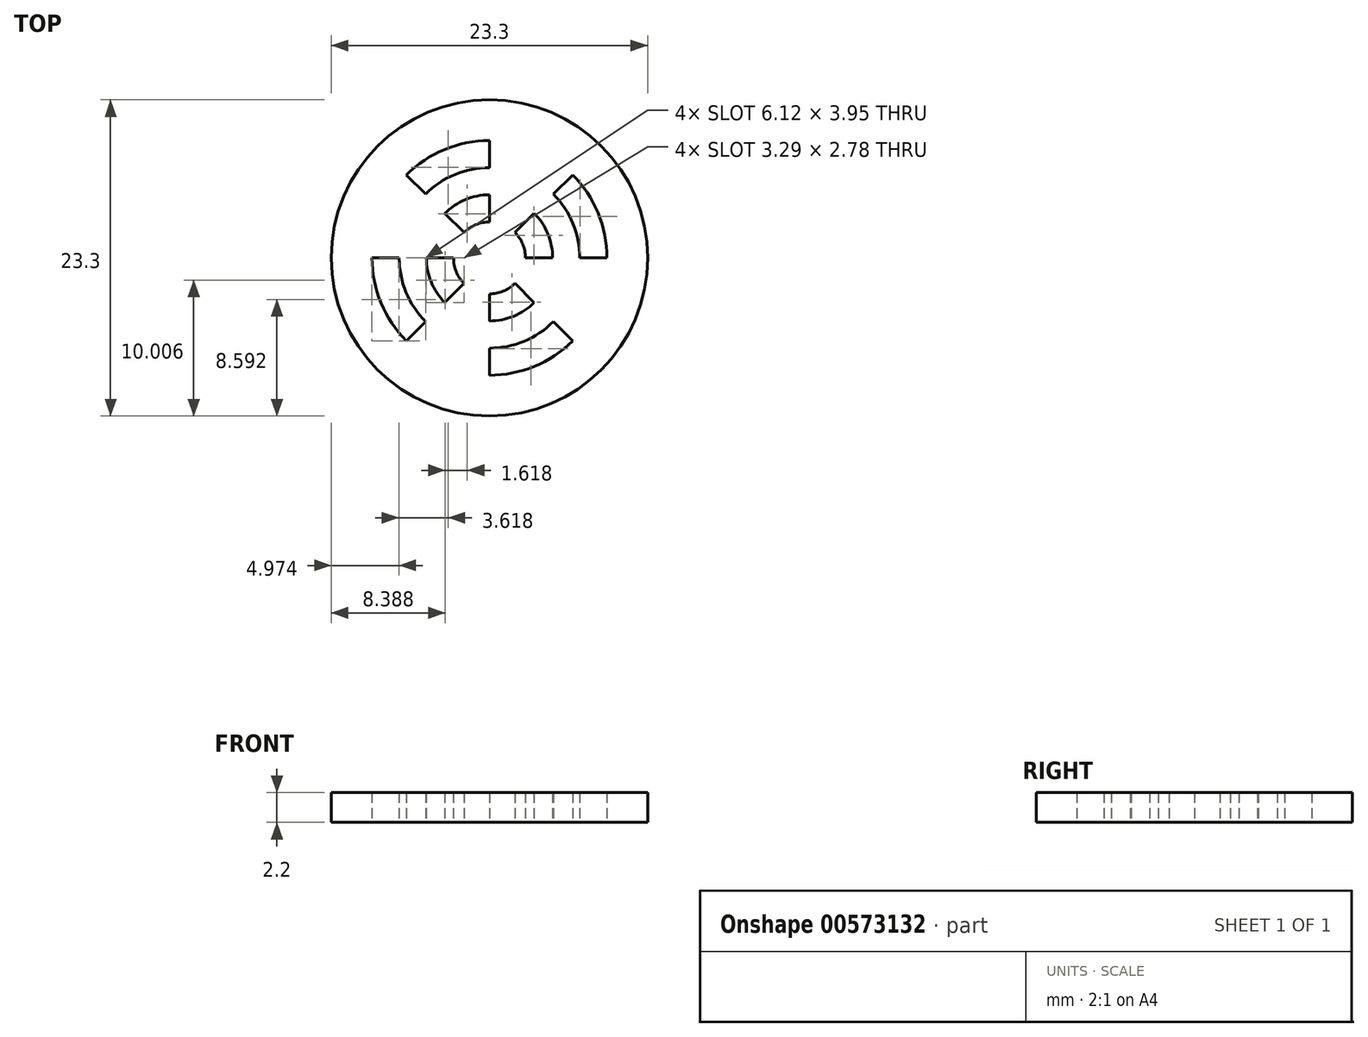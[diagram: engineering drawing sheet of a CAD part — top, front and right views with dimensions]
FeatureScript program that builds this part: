
annotation { "Feature Type Name" : "Feature", "Feature Type Description" : "" }
export const myFeature = defineFeature(function(context is Context, id is Id, definition is map)
    precondition{}
    {
        {
            var Q0;
            Q0=qCreatedBy(makeId("Top.planeOp"),FACE);
            var sketch = newSketch(context, id + "F0", { "sketchPlane" : qUnion([Q0])});
            skCircle(sketch, "E0", {"center": v(0, 0) * mm, "radius": 11.65 * mm});
            skSolve(sketch);
        }
        {
            var Q0;
            Q0=makeQuery(id+"F0.imprint","IMPRINT",FACE,{"disambiguationData":[TD([[makeQuery(id+"F0.imprint","IMPRINT",EDGE,{"derivedFrom":sQuery(id+"F0.wireOp",EDGE,"E0")}),1.0]])]});
            extrude(context, id + "F1", {"entities" : qUnion([Q0]), "depth" : 2.2 * mm, "offsetDistance" : 25 * mm});
        }
        {
            var Q0;
            Q0=makeQuery(id+"F1.opExtrude","CAP_FACE",FACE,{"disambiguationData":[OSD([sQuery(id+"F0.wireOp",EDGE,"E0")])],"isStart":true});
            var sketch = newSketch(context, id + "F2", { "sketchPlane" : qUnion([Q0])});
            skCircle(sketch, "E1", {"center": v(0, 0) * mm, "radius": 10.65 * mm});
            skCircle(sketch, "E2", {"center": v(0, 0) * mm, "radius": 8.65 * mm});
            skCircle(sketch, "E3", {"center": v(0, 0) * mm, "radius": 6.65 * mm});
            skCircle(sketch, "E4", {"center": v(0, 0) * mm, "radius": 4.65 * mm});
            skCircle(sketch, "E5", {"center": v(0, 0) * mm, "radius": 2.65 * mm});
            skLineSegment(sketch, "E6", {"start": v(-10.65, 0) * mm, "end": v(10.65, 0) * mm});
            skLineSegment(sketch, "E7", {"start": v(0, -10.65) * mm, "end": v(0, 10.65) * mm});
            skLineSegment(sketch, "E8", {"start": v(-10.65, 0) * mm, "end": v(0, 10.65) * mm, "construction": true});
            skLineSegment(sketch, "E9", {"start": v(-5.33, 5.33) * mm, "end": v(-9.71, 9.71) * mm, "construction": true});
            skLineSegment(sketch, "E10", {"start": v(-8.24, 8.24) * mm, "end": v(8.24, -8.24) * mm, "construction": true});
            skLineSegment(sketch, "E11", {"start": v(0, 0) * mm, "end": v(-8.24, -8.24) * mm});
            skLineSegment(sketch, "E12", {"start": v(0, 0) * mm, "end": v(7.53, 7.53) * mm});
            skLineSegment(sketch, "E13", {"start": v(7.53, -7.53) * mm, "end": v(-7.53, 7.53) * mm});
            skSolve(sketch);
        }
        {
            var Q0;
            {var subQ0=sQuery(id+"F2.wireOp",EDGE,"E11");var subQ1=sQuery(id+"F2.wireOp",EDGE,"E2");var subQ2=makeQuery(id+"F2.imprint","INTERSECT",VERTEX,{"derivedFrom":[subQ1,subQ0]});Q0=makeQuery(id+"F2.imprint","IMPRINT",FACE,{"disambiguationData":[TD([[makeQuery(id+"F2.imprint","IMPRINT",EDGE,{"disambiguationData":[TD([[subQ2,-1.0]])],"derivedFrom":subQ1}),1.0]])]});}
            var Q1;
            {var subQ0=sQuery(id+"F2.wireOp",EDGE,"E11");var subQ1=sQuery(id+"F2.wireOp",EDGE,"E4");var subQ2=makeQuery(id+"F2.imprint","INTERSECT",VERTEX,{"derivedFrom":[subQ1,subQ0]});Q1=makeQuery(id+"F2.imprint","IMPRINT",FACE,{"disambiguationData":[TD([[makeQuery(id+"F2.imprint","IMPRINT",EDGE,{"disambiguationData":[TD([[subQ2,-1.0]])],"derivedFrom":subQ1}),1.0]])]});}
            var Q2;
            {var subQ0=sQuery(id+"F2.wireOp",EDGE,"E6");var subQ1=sQuery(id+"F2.wireOp",EDGE,"E2");var subQ2=makeQuery(id+"F2.imprint","INTERSECT",VERTEX,{"disambiguationData":[OD(0.0)],"derivedFrom":[subQ1,subQ0]});Q2=makeQuery(id+"F2.imprint","IMPRINT",FACE,{"disambiguationData":[TD([[makeQuery(id+"F2.imprint","IMPRINT",EDGE,{"disambiguationData":[TD([[subQ2,1.0]])],"derivedFrom":subQ1}),1.0]])]});}
            var Q3;
            {var subQ0=sQuery(id+"F2.wireOp",EDGE,"E6");var subQ1=sQuery(id+"F2.wireOp",EDGE,"E4");var subQ2=makeQuery(id+"F2.imprint","INTERSECT",VERTEX,{"disambiguationData":[OD(0.0)],"derivedFrom":[subQ1,subQ0]});Q3=makeQuery(id+"F2.imprint","IMPRINT",FACE,{"disambiguationData":[TD([[makeQuery(id+"F2.imprint","IMPRINT",EDGE,{"disambiguationData":[TD([[subQ2,1.0]])],"derivedFrom":subQ1}),1.0]])]});}
            var Q4;
            {var subQ0=sQuery(id+"F2.wireOp",EDGE,"E12");var subQ1=sQuery(id+"F2.wireOp",EDGE,"E2");var subQ2=makeQuery(id+"F2.imprint","INTERSECT",VERTEX,{"derivedFrom":[subQ1,subQ0]});Q4=makeQuery(id+"F2.imprint","IMPRINT",FACE,{"disambiguationData":[TD([[makeQuery(id+"F2.imprint","IMPRINT",EDGE,{"disambiguationData":[TD([[subQ2,-1.0]])],"derivedFrom":subQ1}),1.0]])]});}
            var Q5;
            {var subQ0=sQuery(id+"F2.wireOp",EDGE,"E12");var subQ1=sQuery(id+"F2.wireOp",EDGE,"E4");var subQ2=makeQuery(id+"F2.imprint","INTERSECT",VERTEX,{"derivedFrom":[subQ1,subQ0]});Q5=makeQuery(id+"F2.imprint","IMPRINT",FACE,{"disambiguationData":[TD([[makeQuery(id+"F2.imprint","IMPRINT",EDGE,{"disambiguationData":[TD([[subQ2,-1.0]])],"derivedFrom":subQ1}),1.0]])]});}
            var Q6;
            {var subQ0=sQuery(id+"F2.wireOp",EDGE,"E13");var subQ1=sQuery(id+"F2.wireOp",EDGE,"E4");var subQ2=makeQuery(id+"F2.imprint","INTERSECT",VERTEX,{"disambiguationData":[OD(0.0)],"derivedFrom":[subQ1,subQ0]});Q6=makeQuery(id+"F2.imprint","IMPRINT",FACE,{"disambiguationData":[TD([[makeQuery(id+"F2.imprint","IMPRINT",EDGE,{"disambiguationData":[TD([[subQ2,-1.0]])],"derivedFrom":subQ1}),1.0]])]});}
            var Q7;
            {var subQ0=sQuery(id+"F2.wireOp",EDGE,"E13");var subQ1=sQuery(id+"F2.wireOp",EDGE,"E2");var subQ2=makeQuery(id+"F2.imprint","INTERSECT",VERTEX,{"disambiguationData":[OD(0.0)],"derivedFrom":[subQ1,subQ0]});Q7=makeQuery(id+"F2.imprint","IMPRINT",FACE,{"disambiguationData":[TD([[makeQuery(id+"F2.imprint","IMPRINT",EDGE,{"disambiguationData":[TD([[subQ2,-1.0]])],"derivedFrom":subQ1}),1.0]])]});}
            extrude(context, id + "F3", {"entities" : qUnion([Q0, Q1, Q2, Q3, Q4, Q5, Q6, Q7]), "operationType" : NewBodyOperationType.REMOVE, "oppositeDirection" : true, "depth" : 25 * mm, "offsetDistance" : 25 * mm});
        }
    });
